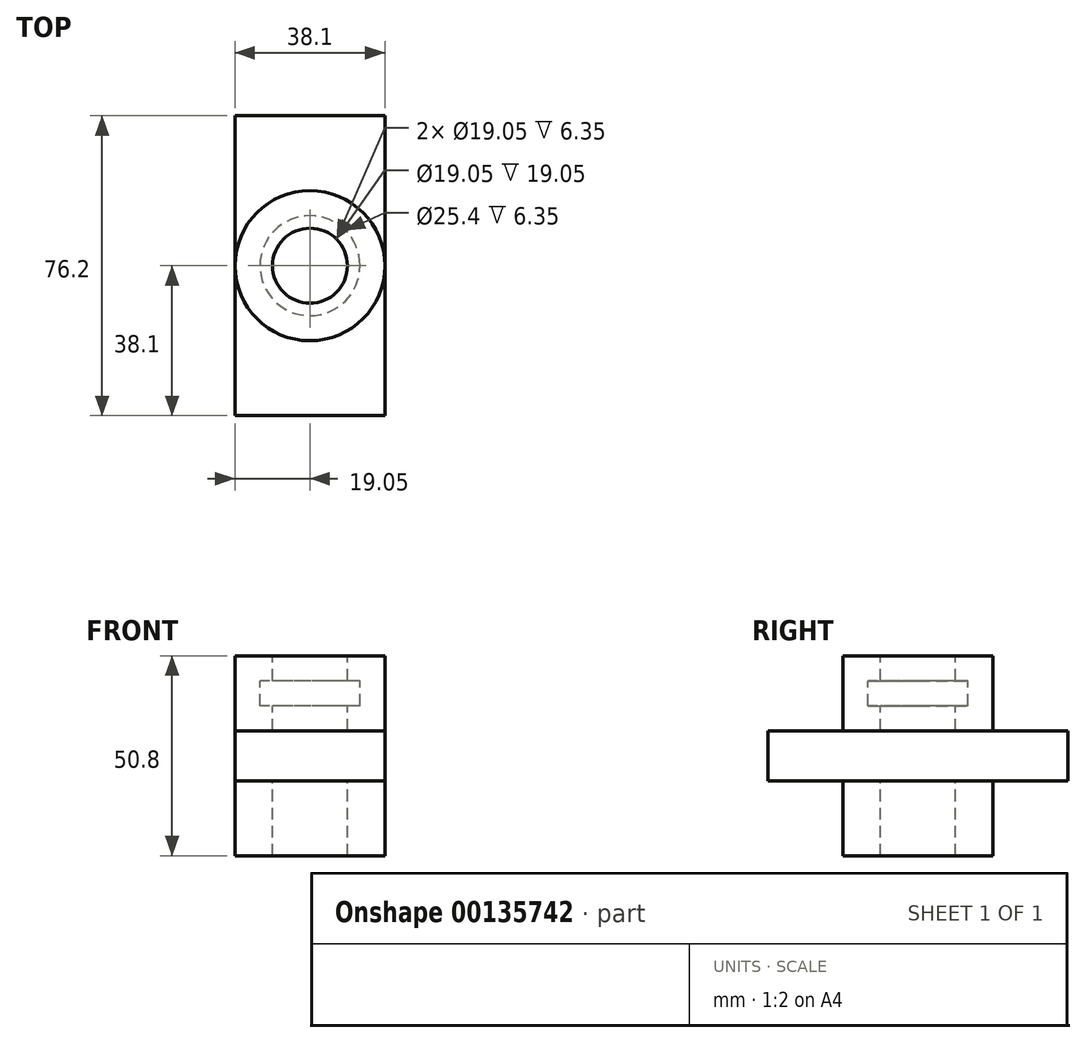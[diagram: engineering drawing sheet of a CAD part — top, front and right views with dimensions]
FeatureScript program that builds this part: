
annotation { "Feature Type Name" : "Feature", "Feature Type Description" : "" }
export const myFeature = defineFeature(function(context is Context, id is Id, definition is map)
    precondition{}
    {
        {
            var Q0;
            Q0=qCreatedBy(makeId("Top.planeOp"),FACE);
            var sketch = newSketch(context, id + "F0", { "sketchPlane" : qUnion([Q0])});
            skCircle(sketch, "E0", {"center": v(0, 0) * mm, "radius": 19.05 * mm});
            skCircle(sketch, "E1", {"center": v(0, 0) * mm, "radius": 9.53 * mm});
            skSolve(sketch);
        }
        {
            var Q0;
            Q0=makeQuery(id+"F0.imprint","IMPRINT",FACE,{"disambiguationData":[TD([[makeQuery(id+"F0.imprint","IMPRINT",EDGE,{"derivedFrom":sQuery(id+"F0.wireOp",EDGE,"E0")}),1.0]])]});
            extrude(context, id + "F1", {"entities" : qUnion([Q0]), "oppositeDirection" : true, "depth" : 50.8 * mm});
        }
        {
            var Q0;
            Q0=qCreatedBy(makeId("Front.planeOp"),FACE);
            cPlane(context, id + "F2", {"entities" : qUnion([Q0]), "cplaneType" : CPlaneType.OFFSET, "offset" : 38.1 * mm, "width" : 152.4 * mm, "height" : 152.4 * mm});
        }
        {
            var Q0;
            Q0=qCreatedBy(id+"F2.planeOp",FACE);
            var sketch = newSketch(context, id + "F3", { "sketchPlane" : qUnion([Q0])});
            skLineSegment(sketch, "E2.bottom", {"start": v(-19.05, 0) * mm, "end": v(19.05, 0) * mm});
            skLineSegment(sketch, "E2.top", {"start": v(-19.05, -50.8) * mm, "end": v(19.05, -50.8) * mm});
            skLineSegment(sketch, "E2.left", {"start": v(-19.05, 0) * mm, "end": v(-19.05, -50.8) * mm});
            skLineSegment(sketch, "E2.right", {"start": v(19.05, 0) * mm, "end": v(19.05, -50.8) * mm});
            skLineSegment(sketch, "E3.bottom", {"start": v(-19.05, -19.05) * mm, "end": v(19.05, -19.05) * mm});
            skLineSegment(sketch, "E3.top", {"start": v(-19.05, -31.75) * mm, "end": v(19.05, -31.75) * mm});
            skLineSegment(sketch, "E3.left", {"start": v(-19.05, -19.05) * mm, "end": v(-19.05, -31.75) * mm});
            skLineSegment(sketch, "E3.right", {"start": v(19.05, -19.05) * mm, "end": v(19.05, -31.75) * mm});
            skSolve(sketch);
        }
        {
            var Q0;
            Q0=makeQuery(id+"F3.imprint","IMPRINT",FACE,{"disambiguationData":[TD([[makeQuery(id+"F3.imprint","IMPRINT",EDGE,{"derivedFrom":sQuery(id+"F3.wireOp",EDGE,"E3.bottom")}),-1.0]])]});
            extrude(context, id + "F4", {"entities" : qUnion([Q0]), "operationType" : NewBodyOperationType.ADD, "oppositeDirection" : true, "depth" : 76.2 * mm});
        }
        {
            var Q0;
            Q0=qCreatedBy(makeId("Top.planeOp"),FACE);
            cPlane(context, id + "F5", {"entities" : qUnion([Q0]), "cplaneType" : CPlaneType.OFFSET, "offset" : 6.35 * mm, "oppositeDirection" : true, "width" : 152.4 * mm, "height" : 152.4 * mm});
        }
        {
            var Q0;
            Q0=qCreatedBy(id+"F5.planeOp",FACE);
            var sketch = newSketch(context, id + "F6", { "sketchPlane" : qUnion([Q0])});
            skCircle(sketch, "E4", {"center": v(0, 0) * mm, "radius": 12.7 * mm});
            skSolve(sketch);
        }
        {
            var Q0;
            Q0 = qSketchRegion(id + "F6", true);
            extrude(context, id + "F7", {"entities" : qUnion([Q0]), "operationType" : NewBodyOperationType.REMOVE, "oppositeDirection" : true, "depth" : 6.35 * mm});
        }
    });
